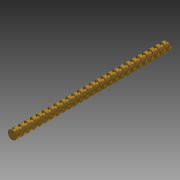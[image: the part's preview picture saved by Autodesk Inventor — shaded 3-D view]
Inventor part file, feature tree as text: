
AUTODESK INVENTOR PART (.ipt)
format: ipt  version: 2014 SP1 (Build 180222100, 222)  size: 336,896 bytes
history: native  units: in
note: dims shown in document units (in); Inventor stores cm internally (conversion verified against a paired STEP export)
features: sketch x2, extrude x1, helix x1
ambient origin geometry x8: Origin, YZ Plane, XZ Plane, XY Plane, X Axis, Y Axis, Z Axis, Center Point
bodies: Solid1 (feature_tree)
feature tree (4):
  extrude  "Extrusion1"  Depth=2.0748in TaperAngle=0.0deg
  helix  "Coil1"  [1 undecoded]
  sketch  "Sketch1"  dims[d0=0.1181in d1=2.0748in d2=0.0in d7=0.0354in]
  sketch  "Sketch3"  dims[d8=0.0394in d9=0.0394in d10=0.0787in d11=0.3937in d12=11.811in d13=0.0in d14=90.0deg d15=90.0deg d16=0.0in d17=0.0in]
note: 1 required parameter value undecoded (feature->parameter linkage not recoverable at this tier; creation-order binding heuristic only, values carry confidence <= 0.55)
